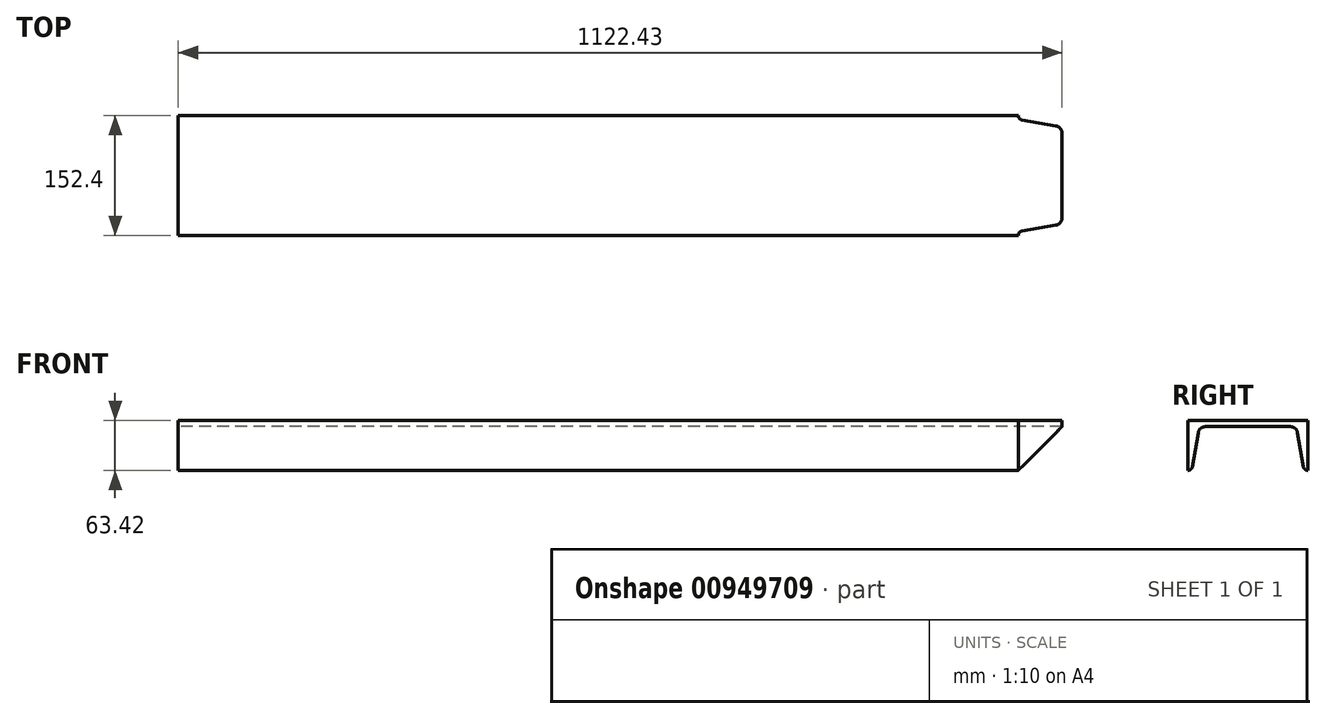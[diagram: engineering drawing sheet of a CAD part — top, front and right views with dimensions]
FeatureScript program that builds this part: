
annotation { "Feature Type Name" : "Feature", "Feature Type Description" : "" }
export const myFeature = defineFeature(function(context is Context, id is Id, definition is map)
    precondition{}
    {
        {
            var Q0;
            Q0=qCreatedBy(makeId("Right.planeOp"),FACE);
            var sketch = newSketch(context, id + "F0", { "sketchPlane" : qUnion([Q0])});
            skLineSegment(sketch, "E0", {"start": v(-76.2, 0) * mm, "end": v(76.2, 0) * mm});
            skLineSegment(sketch, "E1", {"start": v(76.2, 0) * mm, "end": v(76.2, -63.42) * mm});
            skLineSegment(sketch, "E2", {"start": v(-76.2, 0) * mm, "end": v(-76.2, -63.42) * mm});
            skLineSegment(sketch, "E3", {"start": v(-63.12, -15.57) * mm, "end": v(-70.65, -58.76) * mm});
            skLineSegment(sketch, "E4", {"start": v(63.12, -15.57) * mm, "end": v(70.65, -58.76) * mm});
            skLineSegment(sketch, "E5", {"start": v(-53.98, -7.87) * mm, "end": v(53.98, -7.87) * mm});
            skArc(sketch, "E6.filletArc", {"start": v(-76.2, -63.42) * mm, "mid": v(-72.57, -62.1) * mm, "end": v(-70.65, -58.76) * mm});
            skArc(sketch, "E7.filletArc", {"start": v(70.65, -58.76) * mm, "mid": v(72.57, -62.1) * mm, "end": v(76.2, -63.42) * mm});
            skArc(sketch, "E8.filletArc", {"start": v(-53.98, -7.87) * mm, "mid": v(-59.95, -10.05) * mm, "end": v(-63.12, -15.57) * mm});
            skArc(sketch, "E9.filletArc", {"start": v(63.12, -15.57) * mm, "mid": v(59.95, -10.05) * mm, "end": v(53.98, -7.87) * mm});
            skSolve(sketch);
        }
        {
            var Q0;
            Q0=qSketchRegion(id+"F0",true);
            extrude(context, id + "F1", {"entities" : qUnion([Q0]), "depth" : 1130.3 * mm, "offsetDistance" : 25.4 * mm});
        }
        {
            var Q0;
            Q0=makeQuery(id+"F1.opExtrude","SWEPT_FACE",FACE,{"disambiguationData":[OSD([sQuery(id+"F0.wireOp",EDGE,"E0")])]});
            var sketch = newSketch(context, id + "F2", { "sketchPlane" : qUnion([Q0])});
            skLineSegment(sketch, "E10", {"start": v(1130.3, 76.2) * mm, "end": v(1130.3, -76.2) * mm});
            skLineSegment(sketch, "E11", {"start": v(1130.3, -76.2) * mm, "end": v(1066.88, -76.2) * mm});
            skLineSegment(sketch, "E12", {"start": v(1130.3, 76.2) * mm, "end": v(1066.88, 76.2) * mm});
            skLineSegment(sketch, "E13", {"start": v(1114.73, 63.12) * mm, "end": v(1071.54, 70.65) * mm});
            skLineSegment(sketch, "E14", {"start": v(1114.73, -63.12) * mm, "end": v(1071.54, -70.65) * mm});
            skLineSegment(sketch, "E15", {"start": v(1122.43, 53.98) * mm, "end": v(1122.43, -53.98) * mm});
            skArc(sketch, "E16.filletArc", {"start": v(1066.88, 76.2) * mm, "mid": v(1068.2, 72.57) * mm, "end": v(1071.54, 70.65) * mm});
            skArc(sketch, "E17.filletArc", {"start": v(1071.54, -70.65) * mm, "mid": v(1068.2, -72.57) * mm, "end": v(1066.88, -76.2) * mm});
            skArc(sketch, "E18.filletArc", {"start": v(1122.43, 53.98) * mm, "mid": v(1120.25, 59.95) * mm, "end": v(1114.73, 63.12) * mm});
            skArc(sketch, "E19.filletArc", {"start": v(1114.73, -63.12) * mm, "mid": v(1120.25, -59.95) * mm, "end": v(1122.43, -53.98) * mm});
            skSolve(sketch);
        }
        {
            var Q0;
            Q0=qSketchRegion(id+"F2",true);
            extrude(context, id + "F3", {"entities" : qUnion([Q0]), "operationType" : NewBodyOperationType.REMOVE, "endBound" : BoundingType.THROUGH_ALL, "oppositeDirection" : true, "depth" : 25.4 * mm, "offsetDistance" : 25.4 * mm});
        }
    });
